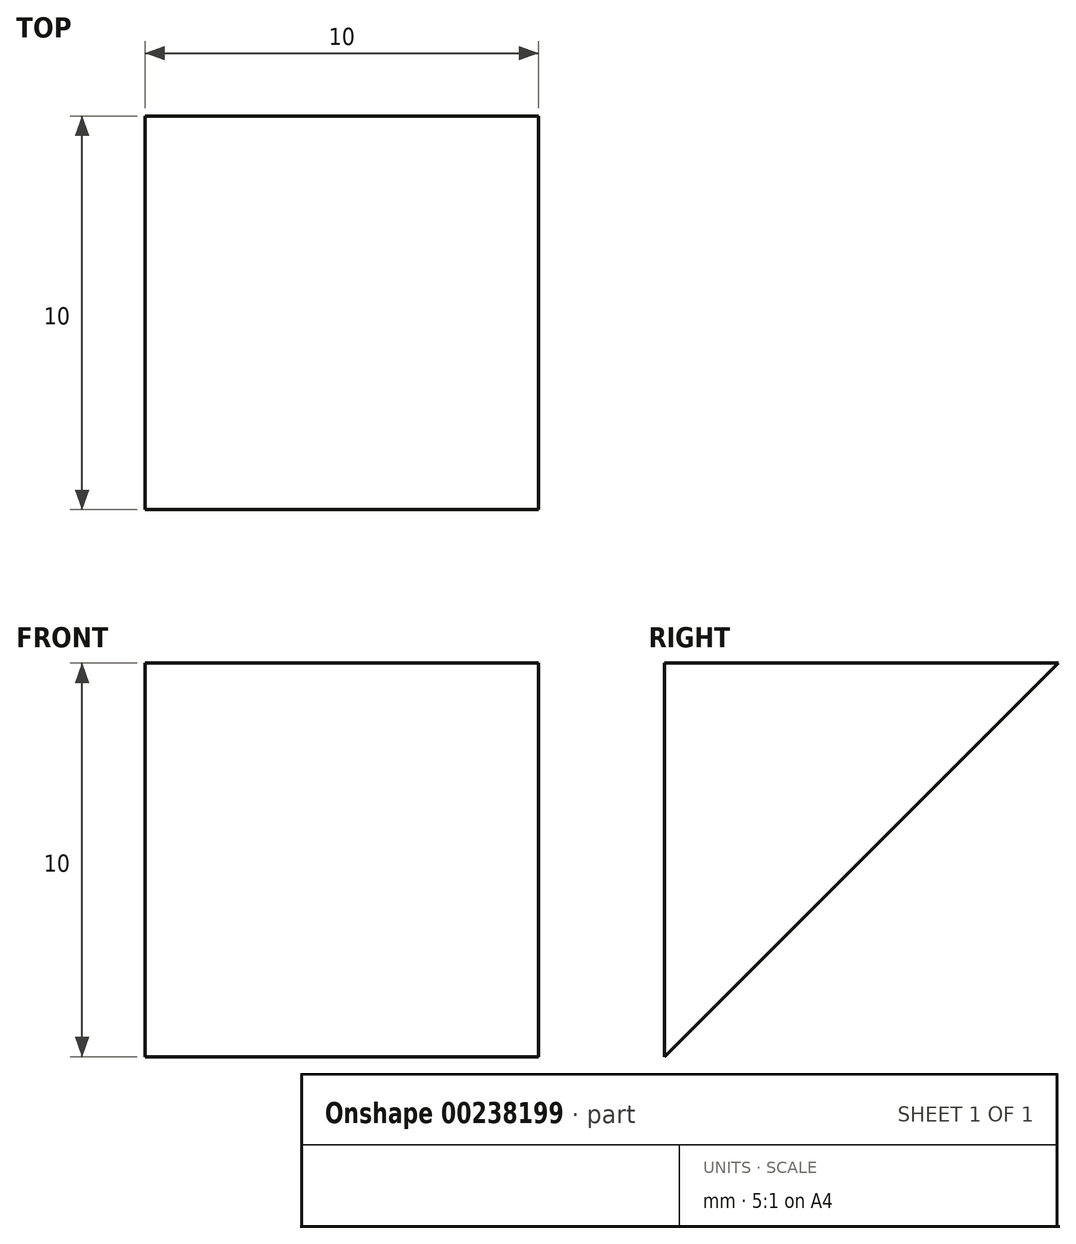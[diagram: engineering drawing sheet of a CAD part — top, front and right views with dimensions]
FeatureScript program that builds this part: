
annotation { "Feature Type Name" : "Feature", "Feature Type Description" : "" }
export const myFeature = defineFeature(function(context is Context, id is Id, definition is map)
    precondition{}
    {
        {
            var Q0;
            Q0=qCreatedBy(makeId("Top.planeOp"),FACE);
            var sketch = newSketch(context, id + "F0", { "sketchPlane" : qUnion([Q0])});
            skLineSegment(sketch, "E0.bottom", {"start": v(-5, -5) * mm, "end": v(5, -5) * mm});
            skLineSegment(sketch, "E0.top", {"start": v(-5, 5) * mm, "end": v(5, 5) * mm});
            skLineSegment(sketch, "E0.left", {"start": v(-5, -5) * mm, "end": v(-5, 5) * mm});
            skLineSegment(sketch, "E0.right", {"start": v(5, -5) * mm, "end": v(5, 5) * mm});
            skPoint(sketch, "E0.middle", {"position": v(0, 0) * mm});
            skSolve(sketch);
        }
        {
            var Q0;
            Q0=makeQuery(id+"F0.imprint","IMPRINT",FACE,{"disambiguationData":[TD([[makeQuery(id+"F0.imprint","IMPRINT",EDGE,{"derivedFrom":sQuery(id+"F0.wireOp",EDGE,"E0.bottom")}),1.0]])]});
            extrude(context, id + "F1", {"entities" : qUnion([Q0]), "depth" : 10 * mm});
        }
        {
            var Q0;
            Q0=makeQuery(id+"F1.opExtrude","CAP_EDGE",EDGE,{"disambiguationData":[OSD([sQuery(id+"F0.wireOp",EDGE,"E0.top")])],"isStart":true});
            chamfer(context, id + "F2", {"entities" : qUnion([Q0]), "width" : 10 * mm, "tangentPropagation" : true});
        }
    });
